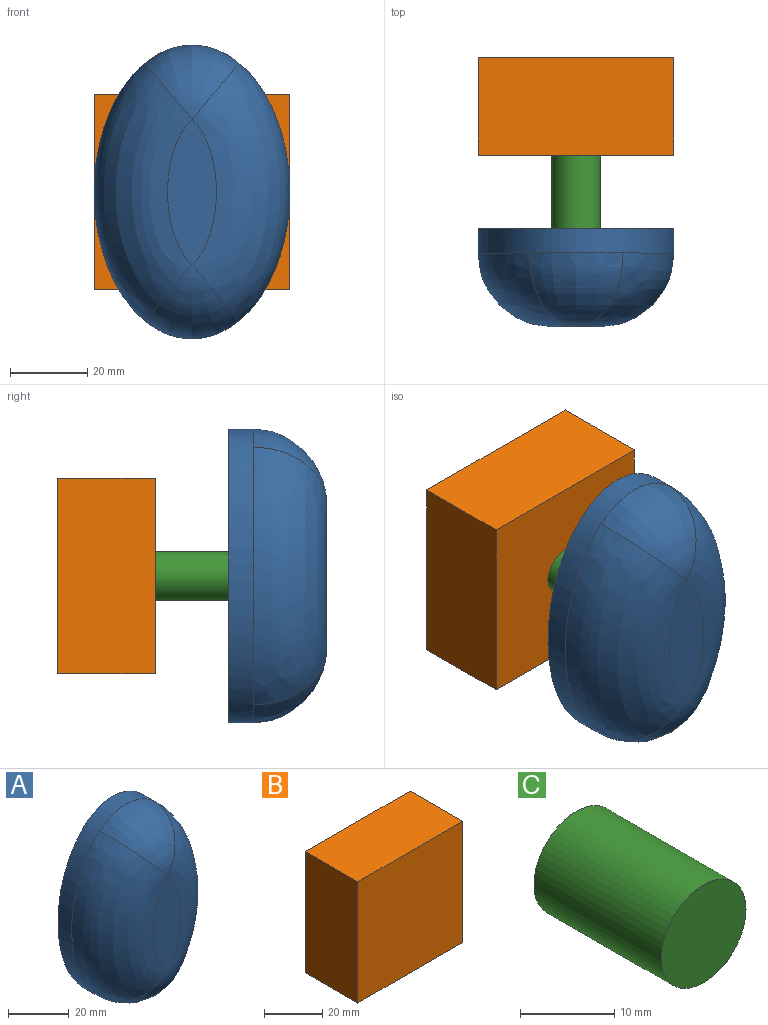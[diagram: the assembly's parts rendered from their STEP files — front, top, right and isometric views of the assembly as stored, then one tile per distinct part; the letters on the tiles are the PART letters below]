
ASSEMBLY  parts=3 mates=3
PART A: 7 faces, bbox 50.8x25.4x76.2 mm
  f0: extruded ~76.2x50.8mm, area 1279.5mm2, adj f2,f3,f4,f5,f6
  f1: plane 37.58x12.7mm, normal (0,-1,0), area 342.2mm2, adj f4,f5
  f2: plane 76.2x50.8mm, normal (0,1,0), area 3040.2mm2, adj f0
  f3: bspline ~24.36x19.32mm, area 321.5mm2, adj f0,f4,f5
  f4: bspline ~68.39x25.52mm, area 1861.9mm2, adj f0,f1,f3,f6
  f5: bspline ~68.24x25.49mm, area 1862.2mm2, adj f0,f1,f3,f6
  f6: bspline ~24.39x19.32mm, area 321.9mm2, adj f0,f4,f5
PART B: 6 faces, bbox 50.8x25.4x50.8 mm
  f0: plane 50.8x25.4mm, normal (0,0,-1), area 1290.3mm2, adj f1,f3,f4,f5
  f1: plane 50.8x25.4mm, normal (1,0,0), area 1290.3mm2, adj f0,f2,f4,f5
  f2: plane 50.8x25.4mm, normal (0,0,1), area 1290.3mm2, adj f1,f3,f4,f5
  f3: plane 50.8x25.4mm, normal (-1,0,0), area 1290.3mm2, adj f0,f2,f4,f5
  f4: plane 50.8x50.8mm, normal (0,-1,0), area 2580.6mm2, adj f0,f1,f2,f3
  f5: plane 50.8x50.8mm, normal (0,1,0), area 2580.6mm2, adj f0,f1,f2,f3
PART C: 3 faces, bbox 12.7x19.1x12.7 mm
  f0: cylinder r=6.35mm len=19.05mm, axis (0,1,0), area 760.1mm2, adj f1,f2
  f1: plane 12.7x12.7mm, normal (0,-1,0), area 126.7mm2, adj f0
  f2: plane 12.7x12.7mm, normal (0,1,0), area 126.7mm2, adj f0
PLACE A t=(-36.36,76.09,57.77)mm
PLACE B t=(-36.36,120.54,57.77)mm
PLACE C t=(-36.36,95.14,57.77)mm
MATE cylindrical C.f0 <-> B.f4  axis (0,1,0) through (-36.36,95.14,57.77)mm
MATE cylindrical C.f0 <-> A.f2  axis (0,1,0) through (-36.36,76.09,57.77)mm
MATE planar A.f2 <-> C.f0  axis (0,1,0) through (-36.36,76.09,57.77)mm
